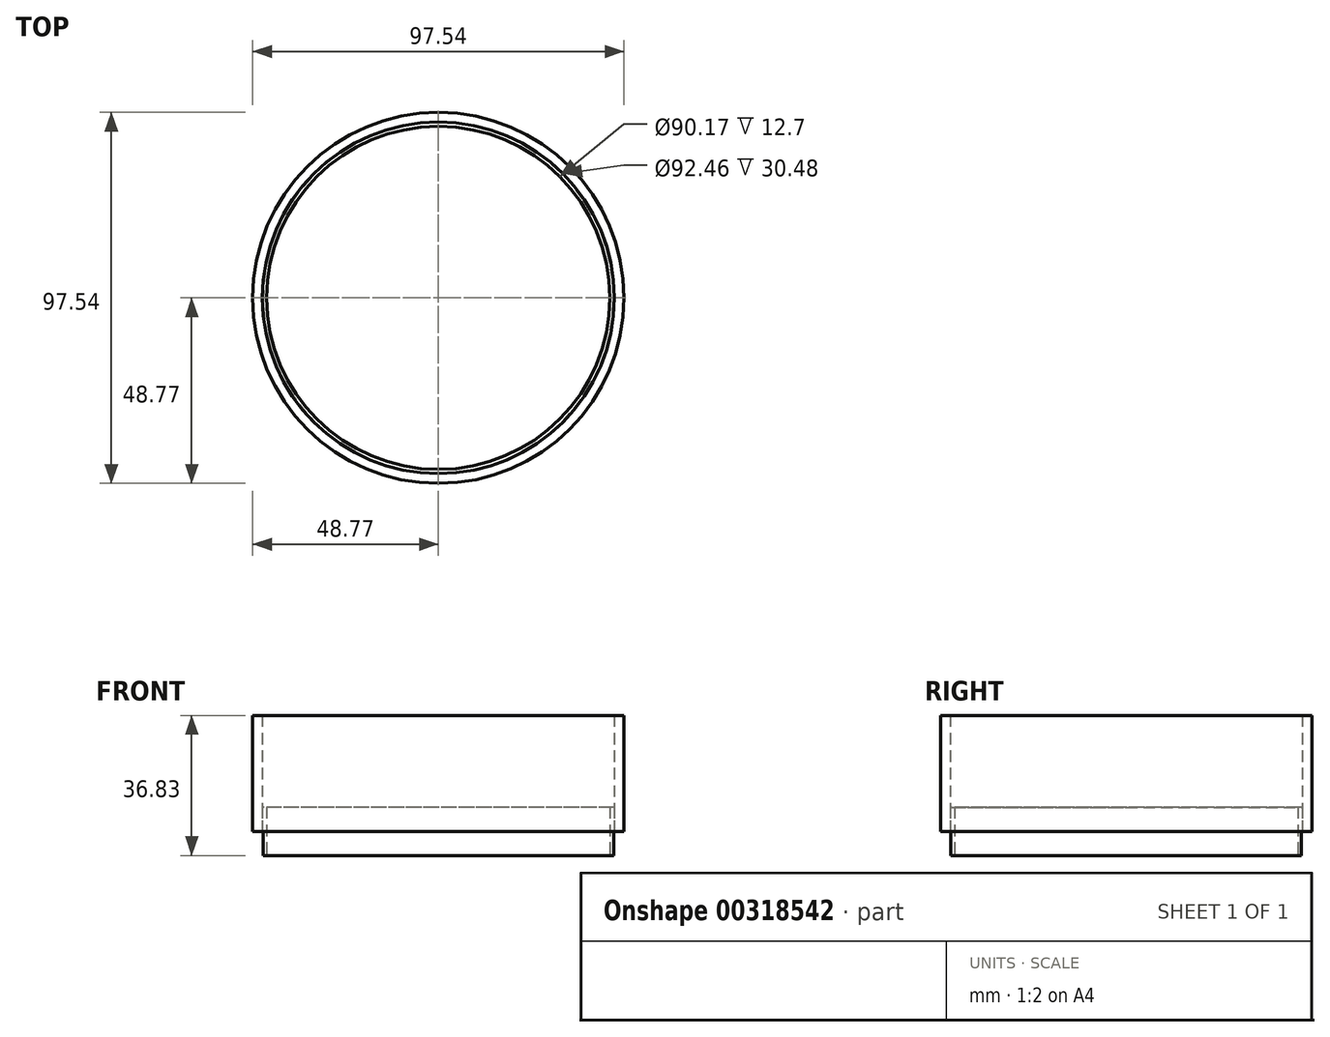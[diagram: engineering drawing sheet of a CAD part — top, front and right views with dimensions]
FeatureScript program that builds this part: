
annotation { "Feature Type Name" : "Feature", "Feature Type Description" : "" }
export const myFeature = defineFeature(function(context is Context, id is Id, definition is map)
    precondition{}
    {
        {
            var Q0;
            Q0=qCreatedBy(makeId("Top.planeOp"),FACE);
            var sketch = newSketch(context, id + "F0", { "sketchPlane" : qUnion([Q0])});
            skCircle(sketch, "E0", {"center": v(0, 0) * mm, "radius": 48.77 * mm});
            skCircle(sketch, "E1", {"center": v(0, 0) * mm, "radius": 46.23 * mm});
            skSolve(sketch);
        }
        {
            var Q0;
            Q0 = qSketchRegion(id + "F0", true);
            extrude(context, id + "F1", {"entities" : qUnion([Q0]), "depth" : 30.48 * mm});
        }
        {
            var Q0;
            Q0=qCreatedBy(makeId("Top.planeOp"),FACE);
            var sketch = newSketch(context, id + "F2", { "sketchPlane" : qUnion([Q0])});
            skCircle(sketch, "E2", {"center": v(0, 0) * mm, "radius": 46.23 * mm});
            skCircle(sketch, "E3", {"center": v(0, 0) * mm, "radius": 45.09 * mm});
            skSolve(sketch);
        }
        {
            var Q0;
            Q0 = qSketchRegion(id + "F2", true);
            extrude(context, id + "F3", {"entities" : qUnion([Q0]), "depth" : 6.35 * mm});
        }
        {
            var Q0;
            Q0=makeQuery(id+"F3.opExtrude","CAP_FACE",FACE,{"disambiguationData":[OSD([sQuery(id+"F2.wireOp",EDGE,"E2"),sQuery(id+"F2.wireOp",EDGE,"E3")])],"isStart":true});
            var sketch = newSketch(context, id + "F4", { "sketchPlane" : qUnion([Q0])});
            skCircle(sketch, "E4", {"center": v(0, 0) * mm, "radius": 45.09 * mm});
            skCircle(sketch, "E5", {"center": v(0, 0) * mm, "radius": 46.04 * mm});
            skSolve(sketch);
        }
        {
            var Q0;
            Q0 = qSketchRegion(id + "F4", true);
            extrude(context, id + "F5", {"entities" : qUnion([Q0]), "operationType" : NewBodyOperationType.ADD, "depth" : 6.35 * mm});
        }
    });
